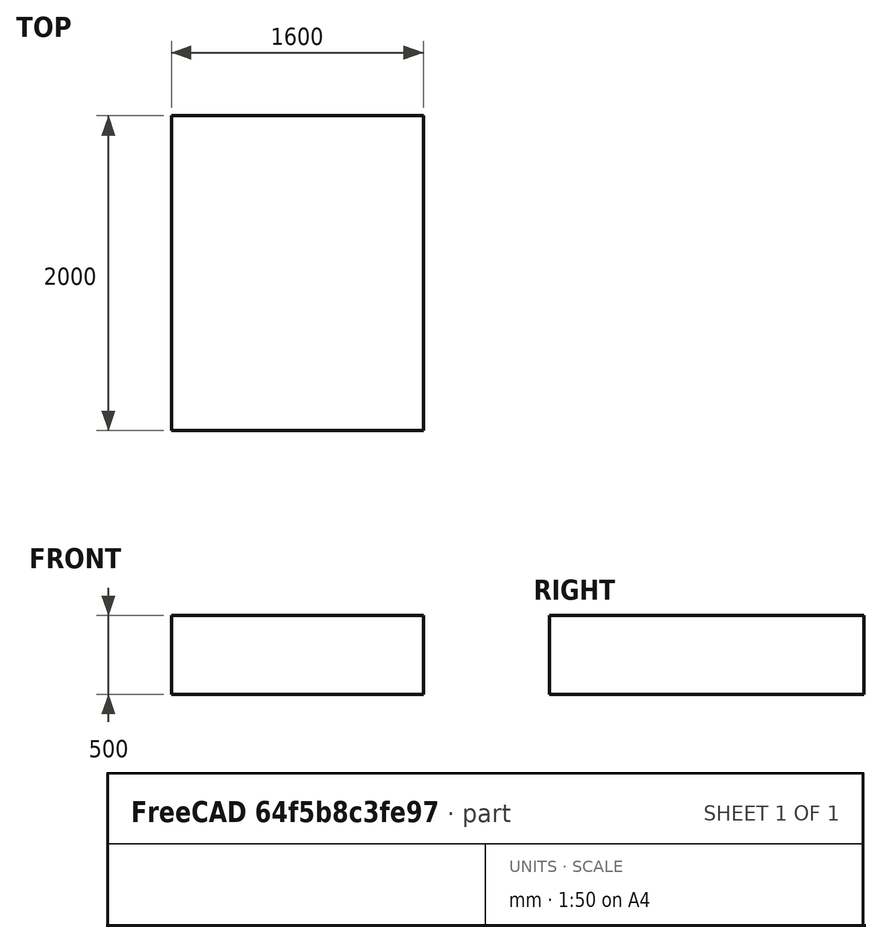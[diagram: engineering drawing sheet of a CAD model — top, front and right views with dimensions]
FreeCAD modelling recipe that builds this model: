
FCSTD DOCUMENT  (FreeCAD 1.0R39109 (Git))
Label: wardrobe
License: All rights reserved
LicenseURL: https://en.wikipedia.org/wiki/All_rights_reserved
objects: Sketcher::SketchObject×1, PartDesign::Pad×1, PartDesign::Body×1
note: 6 computed .brp shape members not serialized (recipe doc carries the construction recipe); baked Part::Feature solids carry a one-line shape summary decoded from their .brp

FEATURE [Sketcher::SketchObject] Sketch
  ArcFitTolerance = 1e-06
  AttachmentSupport = -> [XY_Plane]
  FullyConstrained = true
  MakeInternals = false
  MapMode = 5
  sketch-geometry (8):
    g0: LineSegment StartX=0 StartY=0 StartZ=0 EndX=800 EndY=0 EndZ=0
    g1: LineSegment StartX=800 StartY=0 StartZ=0 EndX=800 EndY=2000 EndZ=0
    g2: LineSegment StartX=800 StartY=2000 StartZ=0 EndX=0 EndY=2000 EndZ=0
    g3: LineSegment StartX=0 StartY=2000 StartZ=0 EndX=0 EndY=0 EndZ=0
    g4: LineSegment StartX=800 StartY=0 StartZ=0 EndX=1600 EndY=0 EndZ=0
    g5: LineSegment StartX=1600 StartY=0 StartZ=0 EndX=1600 EndY=2000 EndZ=0
    g6: LineSegment StartX=1600 StartY=2000 StartZ=0 EndX=800 EndY=2000 EndZ=0
    g7: LineSegment StartX=800 StartY=2000 StartZ=0 EndX=800 EndY=0 EndZ=0
  constraints (22):
    c: Coincident(g0,g1)
    c: Coincident(g1,g2)
    c: Coincident(g2,g3)
    c: Coincident(g3,g0)
    c: Horizontal(g0)
    c: Horizontal(g2)
    c: Vertical(g1)
    c: Vertical(g3)
    c: Coincident(g0,g-1)
    c: Distance(g2) = 800
    c: Distance(g3) = 2000
    c: Coincident(g4,g5)
    c: Coincident(g5,g6)
    c: Coincident(g6,g7)
    c: Coincident(g7,g4)
    c: Horizontal(g4)
    c: Horizontal(g6)
    c: Vertical(g5)
    c: Vertical(g7)
    c: Coincident(g4,g0)
    c: Distance(g6) = 800
    c: Distance(g5) = 2000
FEATURE [PartDesign::Pad] Pad
  Direction = (0,0,1)
  Length = 500
  Length2 = 10
  Profile = -> Sketch
  ReferenceAxis = -> Sketch [N_Axis]
  Refine = true
  Suppressed = false
  Type = 0
FEATURE [PartDesign::Body] Body
  AllowCompound = false
  Group = -> [Sketch,Pad]
  Origin = -> Origin
  Tip = -> Pad
